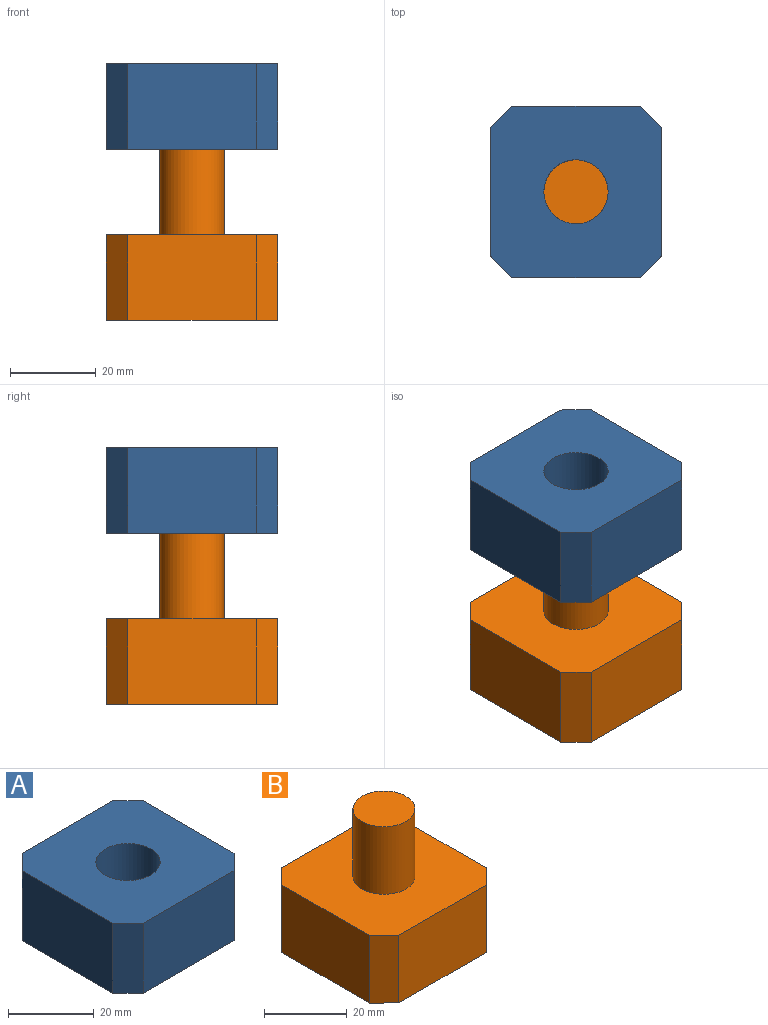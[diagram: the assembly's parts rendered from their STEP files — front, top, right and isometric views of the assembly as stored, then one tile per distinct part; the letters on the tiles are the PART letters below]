
ASSEMBLY  parts=2 mates=1
PART A: 11 faces, bbox 40x40x20 mm
  f0: plane 30x20mm, normal (0,-1,0), area 600mm2, adj f4,f5,f7,f10
  f1: plane 30x20mm, normal (1,0,0), area 600mm2, adj f4,f5,f9,f10
  f2: plane 30x20mm, normal (0,1,0), area 600mm2, adj f4,f5,f8,f9
  f3: plane 30x20mm, normal (-1,0,0), area 600mm2, adj f4,f5,f7,f8
  f4: plane 40x40mm, normal (0,0,1), area 1373.3mm2, adj f0,f1,f2,f3,f6,f7,f8,f9
  f5: plane 40x40mm, normal (0,0,-1), area 1373.3mm2, adj f0,f1,f2,f3,f6,f7,f8,f9
  f6: cylinder r=7.5mm len=20mm, axis (0,0,1), area 942.5mm2, adj f4,f5
  f7: plane 20x5mm, normal (-0.71,-0.71,0), area 141.4mm2, adj f0,f3,f4,f5
  f8: plane 20x5mm, normal (-0.71,0.71,0), area 141.4mm2, adj f2,f3,f4,f5
  f9: plane 20x5mm, normal (0.71,0.71,0), area 141.4mm2, adj f1,f2,f4,f5
  f10: plane 20x5mm, normal (0.71,-0.71,0), area 141.4mm2, adj f0,f1,f4,f5
PART B: 12 faces, bbox 40x40x40 mm
  f0: plane 30x20mm, normal (0,-1,0), area 600mm2, adj f4,f5,f9,f11
  f1: plane 30x20mm, normal (1,0,0), area 600mm2, adj f4,f5,f10,f11
  f2: plane 30x20mm, normal (0,1,0), area 600mm2, adj f4,f5,f8,f10
  f3: plane 30x20mm, normal (-1,0,0), area 600mm2, adj f4,f5,f8,f9
  f4: plane 40x40mm, normal (0,0,1), area 1373.3mm2, adj f0,f1,f2,f3,f6,f8,f9,f10
  f5: plane 40x40mm, normal (0,0,-1), area 1550mm2, adj f0,f1,f2,f3,f8,f9,f10,f11
  f6: cylinder r=7.5mm len=20mm, axis (0,0,-1), area 942.5mm2, adj f4,f7
  f7: plane 15x15mm, normal (0,0,1), area 176.7mm2, adj f6
  f8: plane 20x5mm, normal (-0.71,0.71,0), area 141.4mm2, adj f2,f3,f4,f5
  f9: plane 20x5mm, normal (-0.71,-0.71,0), area 141.4mm2, adj f0,f3,f4,f5
  f10: plane 20x5mm, normal (0.71,0.71,0), area 141.4mm2, adj f1,f2,f4,f5
  f11: plane 20x5mm, normal (0.71,-0.71,0), area 141.4mm2, adj f0,f1,f4,f5
PLACE A rot(axis=(1,0,0),180deg) t=(-11.44,-56.83,102.51)mm
PLACE B rot(axis=(0,0,1),180deg) t=(-11.44,-107.6,42.51)mm fixed
MATE slider B.f6 <-> A.f6  axis (0,0,1) through (-11.44,-56.83,82.51)mm
